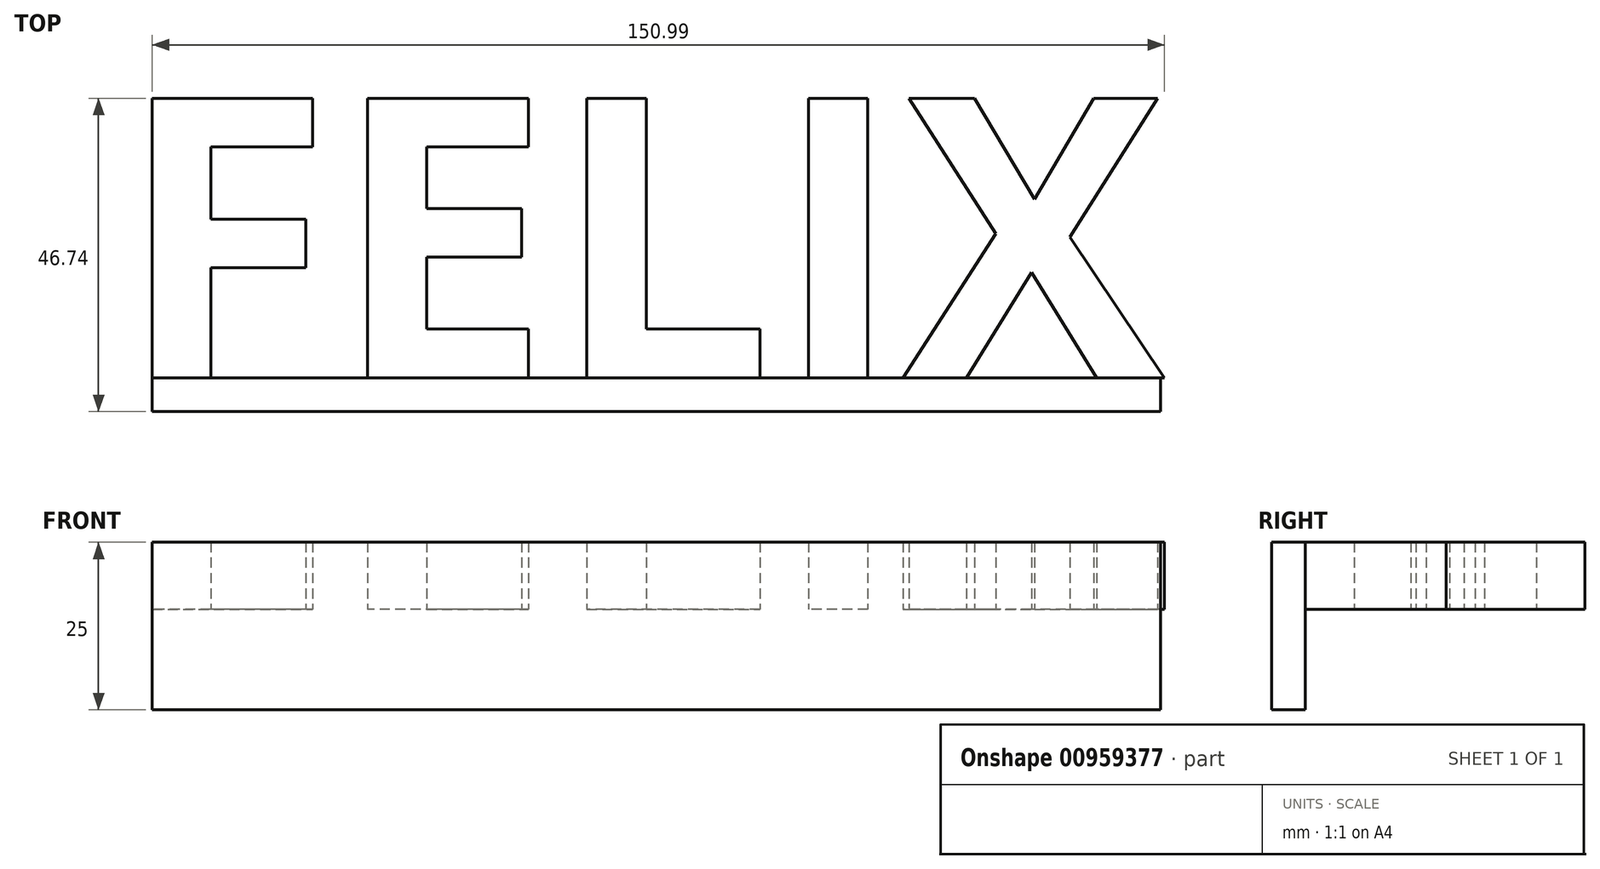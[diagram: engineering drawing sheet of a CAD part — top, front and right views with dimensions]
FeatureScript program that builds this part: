
annotation { "Feature Type Name" : "Feature", "Feature Type Description" : "" }
export const myFeature = defineFeature(function(context is Context, id is Id, definition is map)
    precondition{}
    {
        {
            var Q0;
            Q0=qCreatedBy(makeId("Top.planeOp"),FACE);
            var sketch = newSketch(context, id + "F0", { "sketchPlane" : qUnion([Q0])});
            skText(sketch, "E0", { "text": "FELIX", "fontName": "OpenSans-Bold.ttf"});
            const initialGuessF0  = {"E0": [-0.07848, -0.01835, 1, 0, 0.0421]};
            skSetInitialGuess(sketch, initialGuessF0);
            skSolve(sketch);
        }
        {
            var Q0;
            Q0 = qSketchRegion(id + "F0", true);
            extrude(context, id + "F1", {"entities" : qUnion([Q0]), "depth" : 10 * mm, "offsetDistance" : 25 * mm});
        }
        {
            var Q0;
            Q0=makeQuery(id+"F1.opExtrude","SWEPT_FACE",FACE,{"disambiguationData":[OSD([sQuery(id+"F0.wireOp",EDGE,"E0.sketch_text.stroke-0")])]});
            var sketch = newSketch(context, id + "F2", { "sketchPlane" : qUnion([Q0])});
            skLineSegment(sketch, "E1.bottom", {"start": v(-73.23, 10) * mm, "end": v(77.17, 10) * mm});
            skLineSegment(sketch, "E1.top", {"start": v(-73.23, -15) * mm, "end": v(77.17, -15) * mm});
            skLineSegment(sketch, "E1.left", {"start": v(-73.23, 10) * mm, "end": v(-73.23, -15) * mm});
            skLineSegment(sketch, "E1.right", {"start": v(77.17, 10) * mm, "end": v(77.17, -15) * mm});
            skSolve(sketch);
        }
        {
            var Q0;
            Q0 = qSketchRegion(id + "F2", true);
            extrude(context, id + "F3", {"entities" : qUnion([Q0]), "depth" : 5 * mm, "offsetDistance" : 25 * mm});
        }
    });
